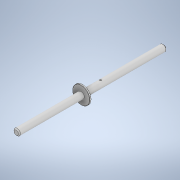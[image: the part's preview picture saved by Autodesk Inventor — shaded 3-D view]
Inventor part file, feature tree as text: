
AUTODESK INVENTOR PART (.ipt)
format: ipt  version: 2022 (Build 260153000, 153)  size: 125,952 bytes
history: native  units: mm
features: chamfer x2, sketch x2, revolve x1, extrude x1
ambient origin geometry x8: Origin, YZ Plane, XZ Plane, XY Plane, X Axis, Y Axis, Z Axis, Center Point
bodies: Solid1 (feature_tree)
feature tree (6):
  revolve  "Revolution1"  [1 undecoded]
  extrude  "Extrusion1"  Depth=150.0mm
  chamfer  "Chamfer1"  Distance=6.0mm
  chamfer  "Chamfer2"  Angle=90.0deg  [1 undecoded]
  sketch  "Sketch1"  dims[d0=120.0mm d1=3.0mm]
  sketch  "Sketch3"  dims[d2=10.0mm d3=150.0mm d4=6.0mm d5=90.0deg d6=3.0mm d7=33.0mm d8=10.0mm d9=0.0mm d10=2.0mm d11=2.0mm d12=45.0deg d13=0.5mm d14=2.0mm d15=45.0deg]
note: 2 required parameter values undecoded (feature->parameter linkage not recoverable at this tier; creation-order binding heuristic only, values carry confidence <= 0.55)